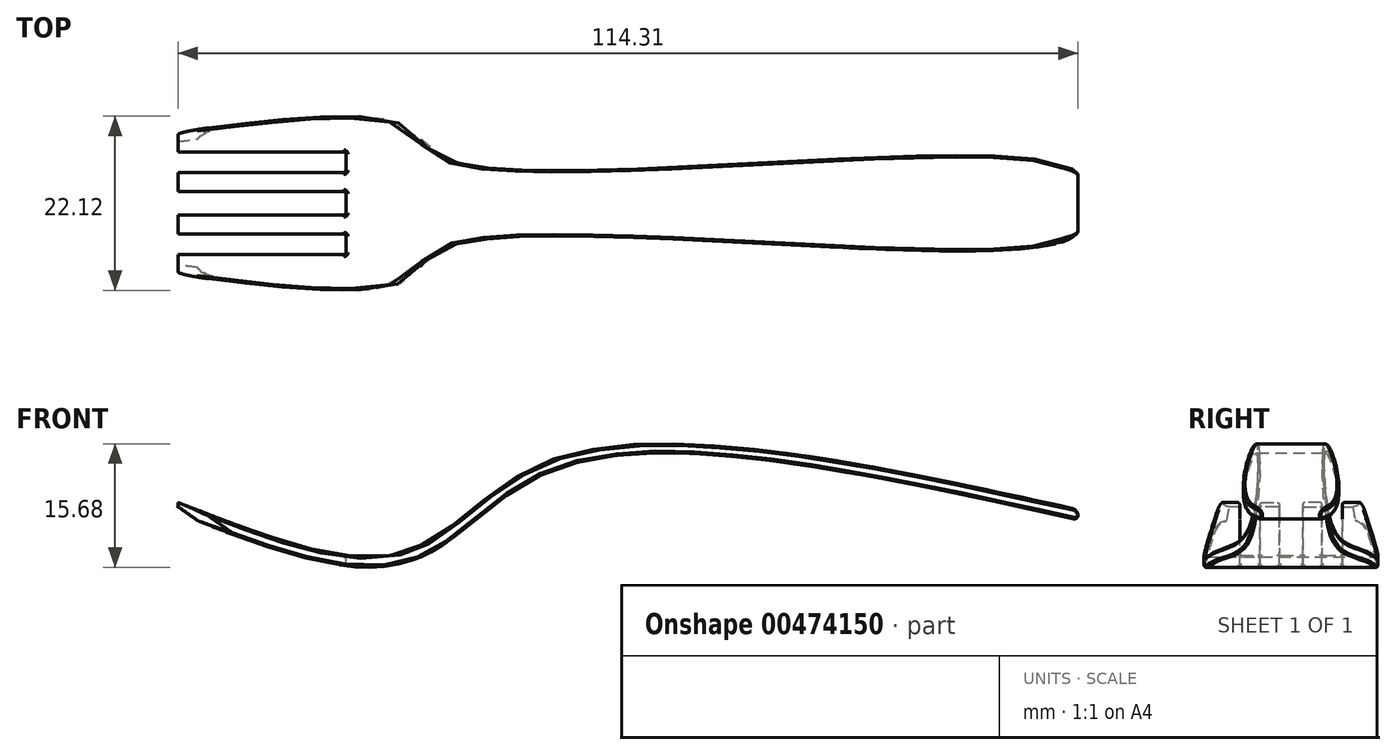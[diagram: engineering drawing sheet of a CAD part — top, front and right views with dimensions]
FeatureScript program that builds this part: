
annotation { "Feature Type Name" : "Feature", "Feature Type Description" : "" }
export const myFeature = defineFeature(function(context is Context, id is Id, definition is map)
    precondition{}
    {
        {
            var Q0;
            Q0=qCreatedBy(makeId("Front.planeOp"),FACE);
            var sketch = newSketch(context, id + "F0", { "sketchPlane" : qUnion([Q0])});
            skFitSpline(sketch, "E0", {"points": [v(-47.75, 0) * mm, v(-21.4, -5.34) * mm, v(-2.94, 6.28) * mm, v(64.35, 0) * mm], "startDerivative": vector(101.26, -39.04) * mm, "endDerivative": vector(175.05, -38.41) * mm});
            skFitSpline(sketch, "E1.0", {"points": [v(-48.2, -1.19) * mm, v(-46.1, -2) * mm, v(-41.86, -3.63) * mm, v(-36.66, -5.38) * mm, v(-32.63, -6.43) * mm, v(-29.68, -6.99) * mm, v(-26.83, -7.27) * mm, v(-24.54, -7.22) * mm, v(-22.77, -6.99) * mm, v(-21.48, -6.7) * mm, v(-20.23, -6.3) * mm, v(-18.65, -5.64) * mm, v(-16.8, -4.59) * mm, v(-14.7, -3.1) * mm, v(-12.68, -1.47) * mm, v(-10.64, 0.2) * mm, v(-8.51, 1.82) * mm, v(-6.24, 3.33) * mm, v(-4.16, 4.42) * mm, v(-2.36, 5.16) * mm, v(-0.44, 5.8) * mm, v(2.2, 6.42) * mm, v(6.85, 7.07) * mm, v(13.44, 7.25) * mm, v(22.36, 6.6) * mm, v(32.09, 5.25) * mm, v(42.41, 3.38) * mm, v(53.14, 1.16) * mm, v(60.43, -0.44) * mm, v(64.07, -1.24) * mm]});
            skLineSegment(sketch, "E2", {"start": v(-47.75, 0) * mm, "end": v(-48.2, -1.19) * mm});
            skLineSegment(sketch, "E3", {"start": v(64.35, 0) * mm, "end": v(64.07, -1.24) * mm});
            skSolve(sketch);
        }
        {
            var Q0;
            Q0=makeQuery(id+"F0.imprint","IMPRINT",FACE,{"disambiguationData":[TD([[makeQuery(id+"F0.imprint","IMPRINT",EDGE,{"derivedFrom":sQuery(id+"F0.wireOp",EDGE,"E0")}),-1.0]])]});
            extrude(context, id + "F1", {"entities" : qUnion([Q0]), "endBound" : BoundingType.SYMMETRIC, "depth" : 25.4 * mm});
        }
        {
            var Q0;
            Q0=qCreatedBy(makeId("Top.planeOp"),FACE);
            var sketch = newSketch(context, id + "F2", { "sketchPlane" : qUnion([Q0])});
            skLineSegment(sketch, "E4", {"start": v(-28.87, 0) * mm, "end": v(-28.87, -1.48) * mm});
            skLineSegment(sketch, "E5", {"start": v(-28.87, -1.48) * mm, "end": v(-50.18, -1.48) * mm});
            skLineSegment(sketch, "E6", {"start": v(-50.18, -1.48) * mm, "end": v(-50.18, -3.93) * mm});
            skLineSegment(sketch, "E7", {"start": v(-50.18, -3.93) * mm, "end": v(-28.87, -3.93) * mm});
            skLineSegment(sketch, "E8", {"start": v(-28.87, -3.93) * mm, "end": v(-28.87, -6.51) * mm});
            skLineSegment(sketch, "E9", {"start": v(-28.87, -6.51) * mm, "end": v(-50.18, -6.51) * mm});
            skLineSegment(sketch, "E10", {"start": v(-50.18, -6.51) * mm, "end": v(-50.18, -9.1) * mm});
            skFitSpline(sketch, "E11", {"points": [v(64.37, 0) * mm, v(62.69, -4.7) * mm, v(-15.06, -5.22) * mm, v(-21.38, -9.87) * mm, v(-50.18, -9.1) * mm], "startDerivative": vector(10.42, -46.86) * mm, "endDerivative": vector(-132.24, 16.67) * mm});
            skLineSegment(sketch, "E12", {"start": v(-28.87, 0) * mm, "end": v(64.37, 0) * mm});
            skLineSegment(sketch, "E13.MirrorCS", {"start": v(-28.87, 1.48) * mm, "end": v(-50.18, 1.48) * mm});
            skLineSegment(sketch, "E14.MirrorCS", {"start": v(-28.87, 0) * mm, "end": v(-28.87, 1.48) * mm});
            skLineSegment(sketch, "E15.MirrorCS", {"start": v(-28.87, 6.51) * mm, "end": v(-50.18, 6.51) * mm});
            skLineSegment(sketch, "E16.MirrorCS", {"start": v(-28.87, 3.93) * mm, "end": v(-28.87, 6.51) * mm});
            skLineSegment(sketch, "E17.MirrorCS", {"start": v(-50.18, 6.51) * mm, "end": v(-50.18, 9.1) * mm});
            skFitSpline(sketch, "E18.MirrorCS", {"points": [v(64.37, 0) * mm, v(62.69, 4.7) * mm, v(-15.06, 5.22) * mm, v(-21.38, 9.87) * mm, v(-50.18, 9.1) * mm], "startDerivative": vector(10.42, 46.86) * mm, "endDerivative": vector(-132.24, -16.67) * mm});
            skLineSegment(sketch, "E19.MirrorCS", {"start": v(-50.18, 1.48) * mm, "end": v(-50.18, 3.93) * mm});
            skLineSegment(sketch, "E20.MirrorCS", {"start": v(-50.18, 3.93) * mm, "end": v(-28.87, 3.93) * mm});
            skLineSegment(sketch, "E21.bottom", {"start": v(-58.53, -33.23) * mm, "end": v(72.87, -33.23) * mm});
            skLineSegment(sketch, "E21.top", {"start": v(-58.53, 32.8) * mm, "end": v(72.87, 32.8) * mm});
            skLineSegment(sketch, "E21.left", {"start": v(-58.53, -33.23) * mm, "end": v(-58.53, 32.8) * mm});
            skLineSegment(sketch, "E21.right", {"start": v(72.87, -33.23) * mm, "end": v(72.87, 32.8) * mm});
            skSolve(sketch);
        }
        {
            var Q0;
            Q0=makeQuery(id+"F1.opExtrude","SWEPT_FACE",FACE,{"disambiguationData":[OSD([sQuery(id+"F0.wireOp",EDGE,"E2")])]});
            extrude(context, id + "F3", {"entities" : qUnion([Q0]), "operationType" : NewBodyOperationType.ADD, "depth" : 9.14 * mm});
        }
        {
            var Q0;
            Q0=makeQuery(id+"F2.imprint","IMPRINT",FACE,{"disambiguationData":[TD([[makeQuery(id+"F2.imprint","IMPRINT",EDGE,{"derivedFrom":sQuery(id+"F2.wireOp",EDGE,"E4")}),-1.0]])]});
            extrude(context, id + "F4", {"entities" : qUnion([Q0]), "operationType" : NewBodyOperationType.REMOVE, "endBound" : BoundingType.SYMMETRIC, "oppositeDirection" : true, "depth" : 50.3 * mm});
        }
        {
            var Q0;
            Q0=makeQuery(id+"F1.opExtrude","SWEPT_EDGE",EDGE,{"disambiguationData":[OSD([sQuery(id+"F0.wireOp",EDGE,"E0"),sQuery(id+"F0.wireOp",EDGE,"E3")])]});
            fillet(context, id + "F5", {"entities" : qUnion([Q0]), "radius" : 1.04 * mm, "tangentPropagation" : true, "allowEdgeOverflow" : false});
        }
        {
            var Q0;
            Q0=makeQuery(id+"F1.opExtrude","SWEPT_EDGE",EDGE,{"disambiguationData":[OSD([sQuery(id+"F0.wireOp",EDGE,"E1.0"),sQuery(id+"F0.wireOp",EDGE,"E3")])]});
            fillet(context, id + "F6", {"entities" : qUnion([Q0]), "radius" : 0.47 * mm, "tangentPropagation" : true, "allowEdgeOverflow" : false});
        }
        {
            var Q0;
            Q0=makeQuery(id+"F4.boolean.opBoolean","INTERSECT",EDGE,{"derivedFrom":[makeQuery(id+"F1.opExtrude","SWEPT_FACE",FACE,{"disambiguationData":[OSD([sQuery(id+"F0.wireOp",EDGE,"E1.0")])]}),makeQuery(id+"F4.opExtrude","SWEPT_FACE",FACE,{"disambiguationData":[OSD([sQuery(id+"F2.wireOp",EDGE,"E11")])]})]});
            fillet(context, id + "F7", {"entities" : qUnion([Q0]), "radius" : 0.2 * mm, "tangentPropagation" : true, "allowEdgeOverflow" : false});
        }
        {
            var Q0;
            Q0=makeQuery(id+"F4.boolean.opBoolean","INTERSECT",EDGE,{"derivedFrom":[makeQuery(id+"F1.opExtrude","SWEPT_FACE",FACE,{"disambiguationData":[OSD([sQuery(id+"F0.wireOp",EDGE,"E0")])]}),makeQuery(id+"F4.opExtrude","SWEPT_FACE",FACE,{"disambiguationData":[OSD([sQuery(id+"F2.wireOp",EDGE,"E18.MirrorCS")])]})]});
            fillet(context, id + "F8", {"entities" : qUnion([Q0]), "radius" : 0.2 * mm, "tangentPropagation" : true, "allowEdgeOverflow" : false});
        }
        {
            var Q0;
            Q0=qCreatedBy(makeId("Front.planeOp"),FACE);
            var sketch = newSketch(context, id + "F9", { "sketchPlane" : qUnion([Q0])});
            skLineSegment(sketch, "E22", {"start": v(-50.3, 0.48) * mm, "end": v(-46.83, -1.96) * mm});
            skLineSegment(sketch, "E23", {"start": v(-50.3, 0.48) * mm, "end": v(-50.3, -1.03) * mm});
            skLineSegment(sketch, "E24", {"start": v(-50.3, -1.03) * mm, "end": v(-46.83, -1.96) * mm});
            skSolve(sketch);
        }
        {
            var Q0;
            Q0=makeQuery(id+"F9.imprint","IMPRINT",FACE,{"disambiguationData":[TD([[makeQuery(id+"F9.imprint","IMPRINT",EDGE,{"derivedFrom":sQuery(id+"F9.wireOp",EDGE,"E22")}),-1.0]])]});
            extrude(context, id + "F10", {"entities" : qUnion([Q0]), "operationType" : NewBodyOperationType.REMOVE, "endBound" : BoundingType.SYMMETRIC, "oppositeDirection" : true, "depth" : 25.4 * mm});
        }
        {
            var Q0;
            Q0=makeQuery(id+"F10.boolean.opBoolean","INTERSECT",EDGE,{"disambiguationData":[OD(3.0)],"derivedFrom":[makeQuery(id+"F1.opExtrude","SWEPT_FACE",FACE,{"disambiguationData":[OSD([sQuery(id+"F0.wireOp",EDGE,"E1.0")])]}),makeQuery(id+"F10.opExtrude","SWEPT_FACE",FACE,{"disambiguationData":[OSD([sQuery(id+"F9.wireOp",EDGE,"E22")])]})]});
            var Q1;
            Q1=makeQuery(id+"F10.boolean.opBoolean","INTERSECT",EDGE,{"disambiguationData":[OD(2.0)],"derivedFrom":[makeQuery(id+"F1.opExtrude","SWEPT_FACE",FACE,{"disambiguationData":[OSD([sQuery(id+"F0.wireOp",EDGE,"E1.0")])]}),makeQuery(id+"F10.opExtrude","SWEPT_FACE",FACE,{"disambiguationData":[OSD([sQuery(id+"F9.wireOp",EDGE,"E22")])]})]});
            var Q2;
            Q2=makeQuery(id+"F10.boolean.opBoolean","INTERSECT",EDGE,{"disambiguationData":[OD(0.0)],"derivedFrom":[makeQuery(id+"F1.opExtrude","SWEPT_FACE",FACE,{"disambiguationData":[OSD([sQuery(id+"F0.wireOp",EDGE,"E1.0")])]}),makeQuery(id+"F10.opExtrude","SWEPT_FACE",FACE,{"disambiguationData":[OSD([sQuery(id+"F9.wireOp",EDGE,"E22")])]})]});
            var Q3;
            Q3=makeQuery(id+"F10.boolean.opBoolean","INTERSECT",EDGE,{"disambiguationData":[OD(1.0)],"derivedFrom":[makeQuery(id+"F1.opExtrude","SWEPT_FACE",FACE,{"disambiguationData":[OSD([sQuery(id+"F0.wireOp",EDGE,"E1.0")])]}),makeQuery(id+"F10.opExtrude","SWEPT_FACE",FACE,{"disambiguationData":[OSD([sQuery(id+"F9.wireOp",EDGE,"E22")])]})]});
            fillet(context, id + "F11", {"entities" : qUnion([Q0, Q1, Q2, Q3]), "radius" : 1.34 * mm, "tangentPropagation" : true, "allowEdgeOverflow" : false});
        }
        {
            var Q0;
            Q0=makeQuery(id+"F4.boolean.opBoolean","INTERSECT",EDGE,{"derivedFrom":[makeQuery(id+"F1.opExtrude","SWEPT_FACE",FACE,{"disambiguationData":[OSD([sQuery(id+"F0.wireOp",EDGE,"E0")])]}),makeQuery(id+"F4.opExtrude","SWEPT_FACE",FACE,{"disambiguationData":[OSD([sQuery(id+"F2.wireOp",EDGE,"E16.MirrorCS")])]})]});
            var Q1;
            Q1=makeQuery(id+"F4.boolean.opBoolean","INTERSECT",EDGE,{"derivedFrom":[makeQuery(id+"F1.opExtrude","SWEPT_FACE",FACE,{"disambiguationData":[OSD([sQuery(id+"F0.wireOp",EDGE,"E0")])]}),makeQuery(id+"F4.opExtrude","SWEPT_FACE",FACE,{"disambiguationData":[OSD([sQuery(id+"F2.wireOp",EDGE,"E4"),sQuery(id+"F2.wireOp",EDGE,"E14.MirrorCS")])]})]});
            var Q2;
            Q2=makeQuery(id+"F4.boolean.opBoolean","INTERSECT",EDGE,{"derivedFrom":[makeQuery(id+"F1.opExtrude","SWEPT_FACE",FACE,{"disambiguationData":[OSD([sQuery(id+"F0.wireOp",EDGE,"E0")])]}),makeQuery(id+"F4.opExtrude","SWEPT_FACE",FACE,{"disambiguationData":[OSD([sQuery(id+"F2.wireOp",EDGE,"E8")])]})]});
            var Q3;
            Q3=makeQuery(id+"F4.boolean.opBoolean","INTERSECT",EDGE,{"derivedFrom":[makeQuery(id+"F1.opExtrude","SWEPT_FACE",FACE,{"disambiguationData":[OSD([sQuery(id+"F0.wireOp",EDGE,"E1.0")])]}),makeQuery(id+"F4.opExtrude","SWEPT_FACE",FACE,{"disambiguationData":[OSD([sQuery(id+"F2.wireOp",EDGE,"E8")])]})]});
            var Q4;
            Q4=makeQuery(id+"F4.boolean.opBoolean","INTERSECT",EDGE,{"derivedFrom":[makeQuery(id+"F1.opExtrude","SWEPT_FACE",FACE,{"disambiguationData":[OSD([sQuery(id+"F0.wireOp",EDGE,"E1.0")])]}),makeQuery(id+"F4.opExtrude","SWEPT_FACE",FACE,{"disambiguationData":[OSD([sQuery(id+"F2.wireOp",EDGE,"E4"),sQuery(id+"F2.wireOp",EDGE,"E14.MirrorCS")])]})]});
            var Q5;
            Q5=makeQuery(id+"F4.boolean.opBoolean","INTERSECT",EDGE,{"derivedFrom":[makeQuery(id+"F1.opExtrude","SWEPT_FACE",FACE,{"disambiguationData":[OSD([sQuery(id+"F0.wireOp",EDGE,"E1.0")])]}),makeQuery(id+"F4.opExtrude","SWEPT_FACE",FACE,{"disambiguationData":[OSD([sQuery(id+"F2.wireOp",EDGE,"E16.MirrorCS")])]})]});
            var Q6;
            Q6=makeQuery(id+"F4.boolean.opBoolean","INTERSECT",EDGE,{"derivedFrom":[makeQuery(id+"F1.opExtrude","SWEPT_FACE",FACE,{"disambiguationData":[OSD([sQuery(id+"F0.wireOp",EDGE,"E0")])]}),makeQuery(id+"F4.opExtrude","SWEPT_FACE",FACE,{"disambiguationData":[OSD([sQuery(id+"F2.wireOp",EDGE,"E13.MirrorCS")])]})]});
            var Q7;
            Q7=makeQuery(id+"F4.boolean.opBoolean","INTERSECT",EDGE,{"derivedFrom":[makeQuery(id+"F1.opExtrude","SWEPT_FACE",FACE,{"disambiguationData":[OSD([sQuery(id+"F0.wireOp",EDGE,"E1.0")])]}),makeQuery(id+"F4.opExtrude","SWEPT_FACE",FACE,{"disambiguationData":[OSD([sQuery(id+"F2.wireOp",EDGE,"E13.MirrorCS")])]})]});
            var Q8;
            Q8=makeQuery(id+"F4.boolean.opBoolean","INTERSECT",EDGE,{"derivedFrom":[makeQuery(id+"F1.opExtrude","SWEPT_FACE",FACE,{"disambiguationData":[OSD([sQuery(id+"F0.wireOp",EDGE,"E0")])]}),makeQuery(id+"F4.opExtrude","SWEPT_FACE",FACE,{"disambiguationData":[OSD([sQuery(id+"F2.wireOp",EDGE,"E5")])]})]});
            var Q9;
            Q9=makeQuery(id+"F4.boolean.opBoolean","INTERSECT",EDGE,{"derivedFrom":[makeQuery(id+"F1.opExtrude","SWEPT_FACE",FACE,{"disambiguationData":[OSD([sQuery(id+"F0.wireOp",EDGE,"E1.0")])]}),makeQuery(id+"F4.opExtrude","SWEPT_FACE",FACE,{"disambiguationData":[OSD([sQuery(id+"F2.wireOp",EDGE,"E5")])]})]});
            var Q10;
            Q10=makeQuery(id+"F4.boolean.opBoolean","INTERSECT",EDGE,{"derivedFrom":[makeQuery(id+"F1.opExtrude","SWEPT_FACE",FACE,{"disambiguationData":[OSD([sQuery(id+"F0.wireOp",EDGE,"E0")])]}),makeQuery(id+"F4.opExtrude","SWEPT_FACE",FACE,{"disambiguationData":[OSD([sQuery(id+"F2.wireOp",EDGE,"E7")])]})]});
            var Q11;
            Q11=makeQuery(id+"F4.boolean.opBoolean","INTERSECT",EDGE,{"derivedFrom":[makeQuery(id+"F1.opExtrude","SWEPT_FACE",FACE,{"disambiguationData":[OSD([sQuery(id+"F0.wireOp",EDGE,"E1.0")])]}),makeQuery(id+"F4.opExtrude","SWEPT_FACE",FACE,{"disambiguationData":[OSD([sQuery(id+"F2.wireOp",EDGE,"E7")])]})]});
            var Q12;
            Q12=makeQuery(id+"F4.boolean.opBoolean","INTERSECT",EDGE,{"derivedFrom":[makeQuery(id+"F1.opExtrude","SWEPT_FACE",FACE,{"disambiguationData":[OSD([sQuery(id+"F0.wireOp",EDGE,"E0")])]}),makeQuery(id+"F4.opExtrude","SWEPT_FACE",FACE,{"disambiguationData":[OSD([sQuery(id+"F2.wireOp",EDGE,"E9")])]})]});
            var Q13;
            Q13=makeQuery(id+"F4.boolean.opBoolean","INTERSECT",EDGE,{"derivedFrom":[makeQuery(id+"F1.opExtrude","SWEPT_FACE",FACE,{"disambiguationData":[OSD([sQuery(id+"F0.wireOp",EDGE,"E1.0")])]}),makeQuery(id+"F4.opExtrude","SWEPT_FACE",FACE,{"disambiguationData":[OSD([sQuery(id+"F2.wireOp",EDGE,"E9")])]})]});
            var Q14;
            Q14=makeQuery(id+"F4.boolean.opBoolean","INTERSECT",EDGE,{"derivedFrom":[makeQuery(id+"F1.opExtrude","SWEPT_FACE",FACE,{"disambiguationData":[OSD([sQuery(id+"F0.wireOp",EDGE,"E0")])]}),makeQuery(id+"F4.opExtrude","SWEPT_FACE",FACE,{"disambiguationData":[OSD([sQuery(id+"F2.wireOp",EDGE,"E15.MirrorCS")])]})]});
            var Q15;
            Q15=makeQuery(id+"F4.boolean.opBoolean","INTERSECT",EDGE,{"derivedFrom":[makeQuery(id+"F1.opExtrude","SWEPT_FACE",FACE,{"disambiguationData":[OSD([sQuery(id+"F0.wireOp",EDGE,"E1.0")])]}),makeQuery(id+"F4.opExtrude","SWEPT_FACE",FACE,{"disambiguationData":[OSD([sQuery(id+"F2.wireOp",EDGE,"E15.MirrorCS")])]})]});
            var Q16;
            Q16=makeQuery(id+"F4.boolean.opBoolean","INTERSECT",EDGE,{"derivedFrom":[makeQuery(id+"F1.opExtrude","SWEPT_FACE",FACE,{"disambiguationData":[OSD([sQuery(id+"F0.wireOp",EDGE,"E1.0")])]}),makeQuery(id+"F4.opExtrude","SWEPT_FACE",FACE,{"disambiguationData":[OSD([sQuery(id+"F2.wireOp",EDGE,"E20.MirrorCS")])]})]});
            var Q17;
            Q17=makeQuery(id+"F4.boolean.opBoolean","INTERSECT",EDGE,{"derivedFrom":[makeQuery(id+"F1.opExtrude","SWEPT_FACE",FACE,{"disambiguationData":[OSD([sQuery(id+"F0.wireOp",EDGE,"E0")])]}),makeQuery(id+"F4.opExtrude","SWEPT_FACE",FACE,{"disambiguationData":[OSD([sQuery(id+"F2.wireOp",EDGE,"E20.MirrorCS")])]})]});
            var Q18;
            Q18=makeQuery(id+"F4.boolean.opBoolean","COPY",EDGE,{"derivedFrom":makeQuery(id+"F4.opExtrude","SWEPT_EDGE",EDGE,{"disambiguationData":[OSD([sQuery(id+"F2.wireOp",EDGE,"E4"),sQuery(id+"F2.wireOp",EDGE,"E5")])]})});
            var Q19;
            Q19=makeQuery(id+"F4.boolean.opBoolean","COPY",EDGE,{"derivedFrom":makeQuery(id+"F4.opExtrude","SWEPT_EDGE",EDGE,{"disambiguationData":[OSD([sQuery(id+"F2.wireOp",EDGE,"E13.MirrorCS"),sQuery(id+"F2.wireOp",EDGE,"E14.MirrorCS")])]})});
            var Q20;
            Q20=makeQuery(id+"F4.boolean.opBoolean","COPY",EDGE,{"derivedFrom":makeQuery(id+"F4.opExtrude","SWEPT_EDGE",EDGE,{"disambiguationData":[OSD([sQuery(id+"F2.wireOp",EDGE,"E7"),sQuery(id+"F2.wireOp",EDGE,"E8")])]})});
            var Q21;
            Q21=makeQuery(id+"F4.boolean.opBoolean","COPY",EDGE,{"derivedFrom":makeQuery(id+"F4.opExtrude","SWEPT_EDGE",EDGE,{"disambiguationData":[OSD([sQuery(id+"F2.wireOp",EDGE,"E8"),sQuery(id+"F2.wireOp",EDGE,"E9")])]})});
            var Q22;
            Q22=makeQuery(id+"F4.boolean.opBoolean","COPY",EDGE,{"derivedFrom":makeQuery(id+"F4.opExtrude","SWEPT_EDGE",EDGE,{"disambiguationData":[OSD([sQuery(id+"F2.wireOp",EDGE,"E16.MirrorCS"),sQuery(id+"F2.wireOp",EDGE,"E15.MirrorCS")])]})});
            var Q23;
            Q23=makeQuery(id+"F4.boolean.opBoolean","COPY",EDGE,{"derivedFrom":makeQuery(id+"F4.opExtrude","SWEPT_EDGE",EDGE,{"disambiguationData":[OSD([sQuery(id+"F2.wireOp",EDGE,"E16.MirrorCS"),sQuery(id+"F2.wireOp",EDGE,"E20.MirrorCS")])]})});
            fillet(context, id + "F12", {"entities" : qUnion([Q0, Q1, Q2, Q3, Q4, Q5, Q6, Q7, Q8, Q9, Q10, Q11, Q12, Q13, Q14, Q15, Q16, Q17, Q18, Q19, Q20, Q21, Q22, Q23]), "radius" : 0.25 * mm, "tangentPropagation" : true, "allowEdgeOverflow" : false});
        }
    });
